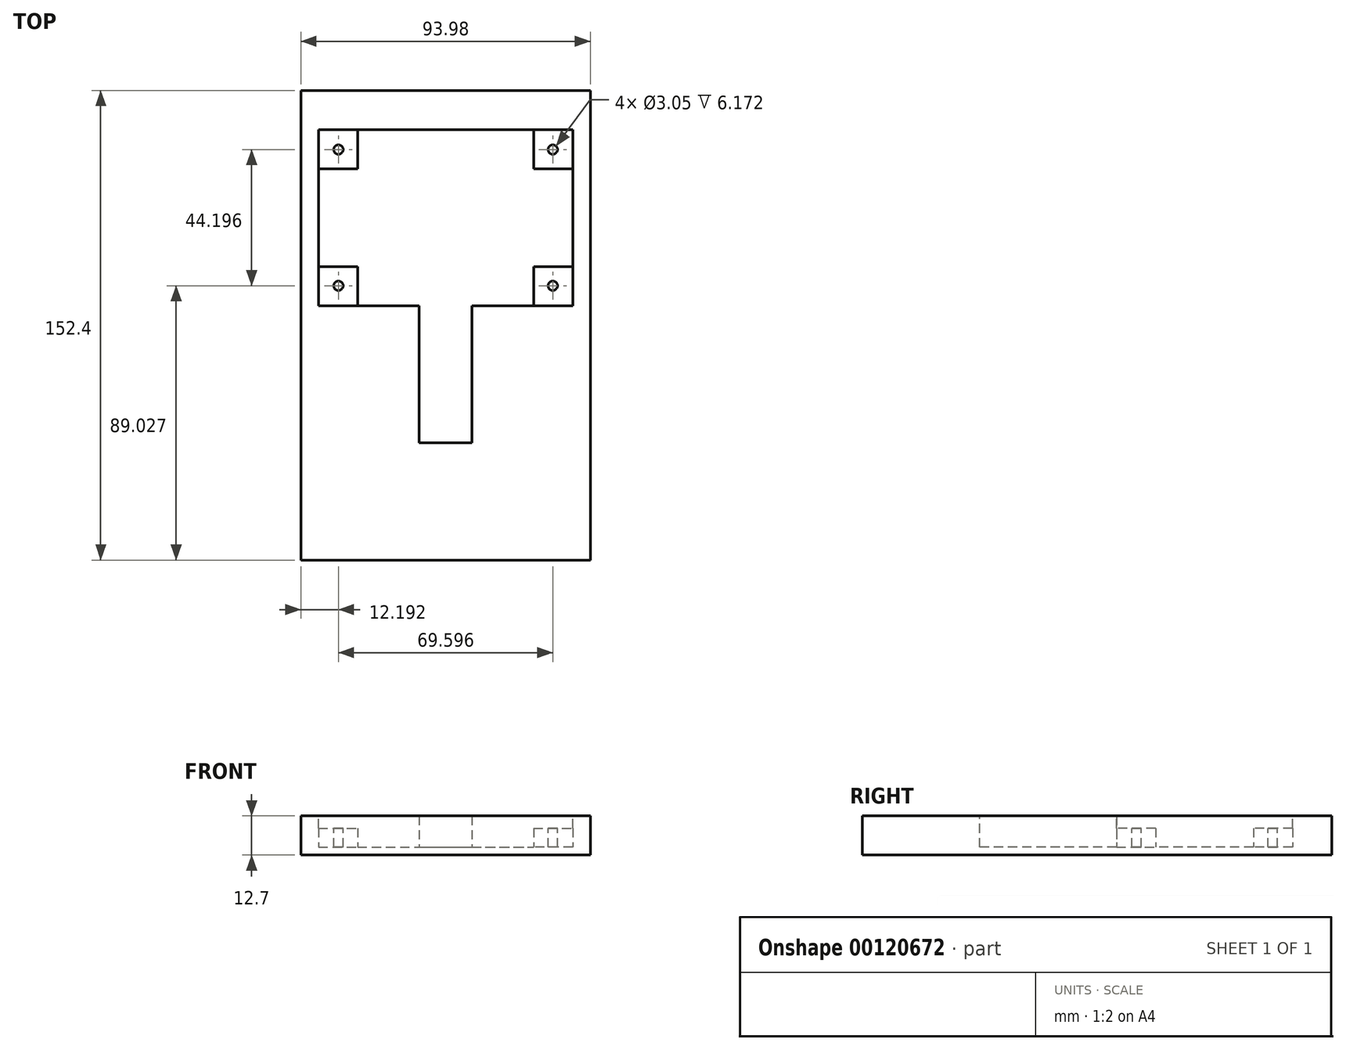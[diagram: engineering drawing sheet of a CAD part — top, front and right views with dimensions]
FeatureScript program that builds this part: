
annotation { "Feature Type Name" : "Feature", "Feature Type Description" : "" }
export const myFeature = defineFeature(function(context is Context, id is Id, definition is map)
    precondition{}
    {
        {
            var Q0;
            Q0=qCreatedBy(makeId("Top.planeOp"),FACE);
            var sketch = newSketch(context, id + "F0", { "sketchPlane" : qUnion([Q0])});
            skLineSegment(sketch, "E0.bottom", {"start": v(0, 0) * mm, "end": v(93.98, 0) * mm});
            skLineSegment(sketch, "E0.top", {"start": v(0, 152.4) * mm, "end": v(93.98, 152.4) * mm});
            skLineSegment(sketch, "E0.left", {"start": v(0, 0) * mm, "end": v(0, 152.4) * mm});
            skLineSegment(sketch, "E0.right", {"start": v(93.98, 0) * mm, "end": v(93.98, 152.4) * mm});
            skSolve(sketch);
        }
        {
            var Q0;
            Q0 = qSketchRegion(id + "F0", true);
            extrude(context, id + "F1", {"entities" : qUnion([Q0]), "oppositeDirection" : true, "depth" : 12.7 * mm});
        }
        {
            var Q0;
            Q0=qCreatedBy(makeId("Top.planeOp"),FACE);
            var sketch = newSketch(context, id + "F2", { "sketchPlane" : qUnion([Q0])});
            skLineSegment(sketch, "E1.bottom", {"start": v(5.71, 139.7) * mm, "end": v(88.27, 139.7) * mm});
            skLineSegment(sketch, "E1.top", {"start": v(5.72, 82.55) * mm, "end": v(88.27, 82.55) * mm});
            skLineSegment(sketch, "E1.left", {"start": v(5.71, 139.7) * mm, "end": v(5.72, 82.55) * mm});
            skLineSegment(sketch, "E1.right", {"start": v(88.27, 139.7) * mm, "end": v(88.27, 82.55) * mm});
            skSolve(sketch);
        }
        {
            var Q0;
            Q0 = qSketchRegion(id + "F2", true);
            extrude(context, id + "F3", {"entities" : qUnion([Q0]), "operationType" : NewBodyOperationType.REMOVE, "oppositeDirection" : true, "depth" : 10.16 * mm});
        }
        {
            var Q0;
            Q0=qCreatedBy(makeId("Top.planeOp"),FACE);
            var sketch = newSketch(context, id + "F4", { "sketchPlane" : qUnion([Q0])});
            skLineSegment(sketch, "E2.bottom", {"start": v(8.89, 136.53) * mm, "end": v(85.1, 136.53) * mm});
            skLineSegment(sketch, "E2.top", {"start": v(8.9, 85.72) * mm, "end": v(85.1, 85.72) * mm});
            skLineSegment(sketch, "E2.left", {"start": v(8.89, 136.53) * mm, "end": v(8.9, 85.72) * mm});
            skLineSegment(sketch, "E2.right", {"start": v(85.1, 136.53) * mm, "end": v(85.1, 85.72) * mm});
            skCircle(sketch, "E3", {"center": v(12.2, 133.22) * mm, "radius": 1.27 * mm});
            skCircle(sketch, "E4", {"center": v(81.79, 133.22) * mm, "radius": 1.27 * mm});
            skCircle(sketch, "E5", {"center": v(12.2, 89.03) * mm, "radius": 1.27 * mm});
            skCircle(sketch, "E6", {"center": v(81.79, 89.03) * mm, "radius": 1.27 * mm});
            skSolve(sketch);
        }
        {
            var Q0;
            Q0=makeQuery(id+"F3.boolean.opBoolean","COPY",FACE,{"derivedFrom":makeQuery(id+"F3.opExtrude","CAP_FACE",FACE,{"disambiguationData":[OSD([sQuery(id+"F2.wireOp",EDGE,"E1.bottom"),sQuery(id+"F2.wireOp",EDGE,"E1.top"),sQuery(id+"F2.wireOp",EDGE,"E1.left"),sQuery(id+"F2.wireOp",EDGE,"E1.right")])],"isStart":false})});
            var sketch = newSketch(context, id + "F5", { "sketchPlane" : qUnion([Q0])});
            skLineSegment(sketch, "E7.bottom", {"start": v(5.71, 139.7) * mm, "end": v(18.41, 139.7) * mm});
            skLineSegment(sketch, "E7.top", {"start": v(5.71, 127) * mm, "end": v(18.41, 127) * mm});
            skLineSegment(sketch, "E7.left", {"start": v(5.71, 139.7) * mm, "end": v(5.71, 127) * mm});
            skLineSegment(sketch, "E7.right", {"start": v(18.41, 139.7) * mm, "end": v(18.41, 127) * mm});
            skLineSegment(sketch, "E8.bottom", {"start": v(88.27, 139.7) * mm, "end": v(75.57, 139.7) * mm});
            skLineSegment(sketch, "E8.top", {"start": v(88.27, 127) * mm, "end": v(75.57, 127) * mm});
            skLineSegment(sketch, "E8.left", {"start": v(88.27, 139.7) * mm, "end": v(88.27, 127) * mm});
            skLineSegment(sketch, "E8.right", {"start": v(75.57, 139.7) * mm, "end": v(75.57, 127) * mm});
            skLineSegment(sketch, "E9.bottom", {"start": v(5.72, 82.55) * mm, "end": v(18.41, 82.55) * mm});
            skLineSegment(sketch, "E9.top", {"start": v(5.71, 95.25) * mm, "end": v(18.41, 95.25) * mm});
            skLineSegment(sketch, "E9.left", {"start": v(5.72, 82.55) * mm, "end": v(5.71, 95.25) * mm});
            skLineSegment(sketch, "E9.right", {"start": v(18.41, 82.55) * mm, "end": v(18.41, 95.25) * mm});
            skLineSegment(sketch, "E10.bottom", {"start": v(88.27, 82.55) * mm, "end": v(75.57, 82.55) * mm});
            skLineSegment(sketch, "E10.top", {"start": v(88.27, 95.25) * mm, "end": v(75.57, 95.25) * mm});
            skLineSegment(sketch, "E10.left", {"start": v(88.27, 82.55) * mm, "end": v(88.27, 95.25) * mm});
            skLineSegment(sketch, "E10.right", {"start": v(75.57, 82.55) * mm, "end": v(75.57, 95.25) * mm});
            skSolve(sketch);
        }
        {
            var Q0;
            Q0 = qSketchRegion(id + "F5", true);
            extrude(context, id + "F6", {"entities" : qUnion([Q0]), "operationType" : NewBodyOperationType.ADD, "depth" : 6.17 * mm});
        }
        {
            var Q0;
            Q0=makeQuery(id+"F6.opExtrude","CAP_FACE",FACE,{"disambiguationData":[OSD([sQuery(id+"F5.wireOp",EDGE,"E7.bottom"),sQuery(id+"F5.wireOp",EDGE,"E7.top"),sQuery(id+"F5.wireOp",EDGE,"E7.left"),sQuery(id+"F5.wireOp",EDGE,"E7.right")])],"isStart":false});
            var sketch = newSketch(context, id + "F7", { "sketchPlane" : qUnion([Q0])});
            skCircle(sketch, "E11", {"center": v(12.2, 133.22) * mm, "radius": 1.52 * mm});
            skCircle(sketch, "E12", {"center": v(81.79, 133.22) * mm, "radius": 1.52 * mm});
            skCircle(sketch, "E13", {"center": v(12.2, 89.03) * mm, "radius": 1.52 * mm});
            skCircle(sketch, "E14", {"center": v(81.79, 89.03) * mm, "radius": 1.52 * mm});
            skSolve(sketch);
        }
        {
            var Q0;
            Q0 = qSketchRegion(id + "F7", true);
            extrude(context, id + "F8", {"entities" : qUnion([Q0]), "operationType" : NewBodyOperationType.REMOVE, "oppositeDirection" : true, "depth" : 6.17 * mm});
        }
        {
            var Q0;
            Q0=makeQuery(id+"F1.opExtrude","CAP_FACE",FACE,{"disambiguationData":[OSD([sQuery(id+"F0.wireOp",EDGE,"E0.bottom"),sQuery(id+"F0.wireOp",EDGE,"E0.top"),sQuery(id+"F0.wireOp",EDGE,"E0.left"),sQuery(id+"F0.wireOp",EDGE,"E0.right")])],"isStart":true});
            var sketch = newSketch(context, id + "F9", { "sketchPlane" : qUnion([Q0])});
            skLineSegment(sketch, "E15.bottom", {"start": v(38.42, 88.9) * mm, "end": v(55.56, 88.9) * mm});
            skLineSegment(sketch, "E15.top", {"start": v(38.42, 38.1) * mm, "end": v(55.56, 38.1) * mm});
            skLineSegment(sketch, "E15.left", {"start": v(38.42, 88.9) * mm, "end": v(38.42, 38.1) * mm});
            skLineSegment(sketch, "E15.right", {"start": v(55.56, 88.9) * mm, "end": v(55.56, 38.1) * mm});
            skSolve(sketch);
        }
        {
            var Q0;
            Q0 = qSketchRegion(id + "F9", true);
            extrude(context, id + "F10", {"entities" : qUnion([Q0]), "operationType" : NewBodyOperationType.REMOVE, "oppositeDirection" : true, "depth" : 10.16 * mm});
        }
    });
